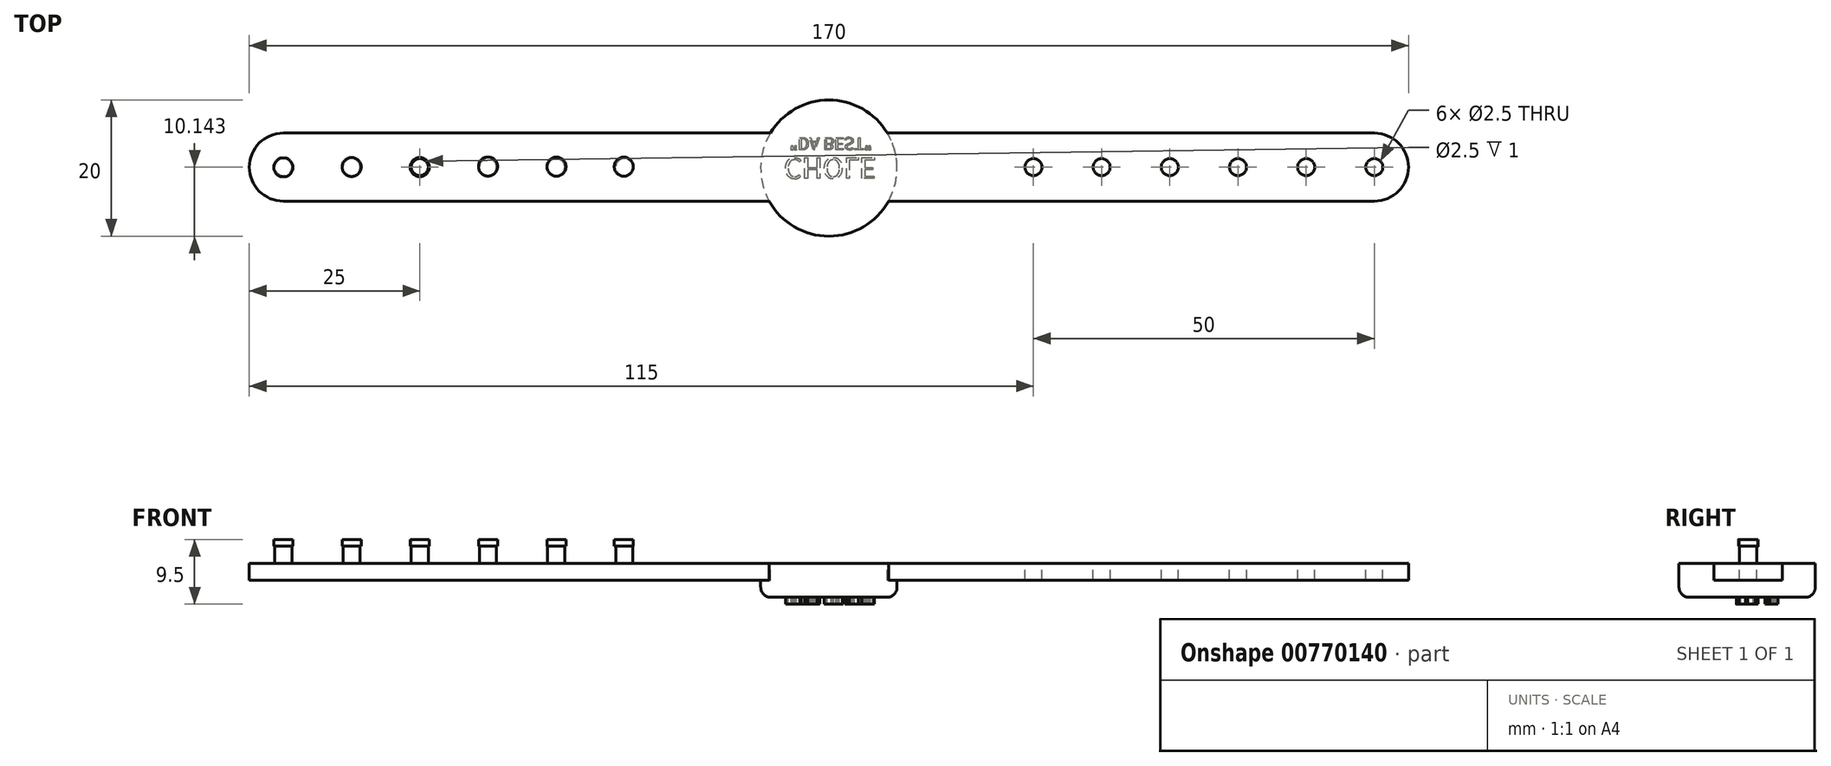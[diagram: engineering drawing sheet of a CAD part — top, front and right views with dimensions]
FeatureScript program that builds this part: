
annotation { "Feature Type Name" : "Feature", "Feature Type Description" : "" }
export const myFeature = defineFeature(function(context is Context, id is Id, definition is map)
    precondition{}
    {
        {
            var Q0;
            Q0=qCreatedBy(makeId("Top.planeOp"),FACE);
            var sketch = newSketch(context, id + "F0", { "sketchPlane" : qUnion([Q0])});
            skLineSegment(sketch, "E0.bottom", {"start": v(-78.4, 24.85) * mm, "end": v(91.6, 24.85) * mm});
            skLineSegment(sketch, "E0.top", {"start": v(-78.4, 14.85) * mm, "end": v(91.6, 14.85) * mm});
            skLineSegment(sketch, "E0.left", {"start": v(-78.4, 24.85) * mm, "end": v(-78.4, 14.85) * mm});
            skLineSegment(sketch, "E0.right", {"start": v(91.6, 24.85) * mm, "end": v(91.6, 14.85) * mm});
            skSolve(sketch);
        }
        {
            var Q0;
            Q0=makeQuery(id+"F0.imprint","IMPRINT",FACE,{"disambiguationData":[TD([[makeQuery(id+"F0.imprint","IMPRINT",EDGE,{"derivedFrom":sQuery(id+"F0.wireOp",EDGE,"E0.bottom")}),-1.0]])]});
            extrude(context, id + "F1", {"entities" : qUnion([Q0]), "depth" : 2.5 * mm, "offsetDistance" : 25 * mm});
        }
        {
            var Q0;
            Q0=makeQuery(id+"F1.opExtrude","SWEPT_EDGE",EDGE,{"disambiguationData":[OSD([sQuery(id+"F0.wireOp",EDGE,"E0.top"),sQuery(id+"F0.wireOp",EDGE,"E0.left")])]});
            var Q1;
            Q1=makeQuery(id+"F1.opExtrude","SWEPT_EDGE",EDGE,{"disambiguationData":[OSD([sQuery(id+"F0.wireOp",EDGE,"E0.bottom"),sQuery(id+"F0.wireOp",EDGE,"E0.left")])]});
            var Q2;
            Q2=makeQuery(id+"F1.opExtrude","SWEPT_EDGE",EDGE,{"disambiguationData":[OSD([sQuery(id+"F0.wireOp",EDGE,"E0.top"),sQuery(id+"F0.wireOp",EDGE,"E0.right")])]});
            var Q3;
            Q3=makeQuery(id+"F1.opExtrude","SWEPT_EDGE",EDGE,{"disambiguationData":[OSD([sQuery(id+"F0.wireOp",EDGE,"E0.bottom"),sQuery(id+"F0.wireOp",EDGE,"E0.right")])]});
            fillet(context, id + "F2", {"entities" : qUnion([Q0, Q1, Q2, Q3]), "radius" : 5 * mm, "tangentPropagation" : true, "allowEdgeOverflow" : false});
        }
        {
            var Q0;
            Q0=makeQuery(id+"F1.opExtrude","CAP_FACE",FACE,{"disambiguationData":[OSD([sQuery(id+"F0.wireOp",EDGE,"E0.bottom"),sQuery(id+"F0.wireOp",EDGE,"E0.top"),sQuery(id+"F0.wireOp",EDGE,"E0.left"),sQuery(id+"F0.wireOp",EDGE,"E0.right")])],"isStart":false});
            var sketch = newSketch(context, id + "F3", { "sketchPlane" : qUnion([Q0])});
            skCircle(sketch, "E1", {"center": v(86.6, 19.85) * mm, "radius": 1.25 * mm});
            skCircle(sketch, "E2", {"center": v(76.6, 19.85) * mm, "radius": 1.25 * mm});
            skCircle(sketch, "E3", {"center": v(66.6, 19.85) * mm, "radius": 1.25 * mm});
            skCircle(sketch, "E4", {"center": v(56.6, 19.85) * mm, "radius": 1.25 * mm});
            skCircle(sketch, "E5", {"center": v(46.6, 19.85) * mm, "radius": 1.25 * mm});
            skCircle(sketch, "E6", {"center": v(36.6, 19.85) * mm, "radius": 1.25 * mm});
            skSolve(sketch);
        }
        {
            var Q0;
            Q0=makeQuery(id+"F3.imprint","IMPRINT",FACE,{"disambiguationData":[TD([[makeQuery(id+"F3.imprint","IMPRINT",EDGE,{"derivedFrom":sQuery(id+"F3.wireOp",EDGE,"E1")}),1.0]])]});
            var Q1;
            Q1=makeQuery(id+"F3.imprint","IMPRINT",FACE,{"disambiguationData":[TD([[makeQuery(id+"F3.imprint","IMPRINT",EDGE,{"derivedFrom":sQuery(id+"F3.wireOp",EDGE,"E2")}),1.0]])]});
            var Q2;
            Q2=makeQuery(id+"F3.imprint","IMPRINT",FACE,{"disambiguationData":[TD([[makeQuery(id+"F3.imprint","IMPRINT",EDGE,{"derivedFrom":sQuery(id+"F3.wireOp",EDGE,"E3")}),1.0]])]});
            var Q3;
            Q3=makeQuery(id+"F3.imprint","IMPRINT",FACE,{"disambiguationData":[TD([[makeQuery(id+"F3.imprint","IMPRINT",EDGE,{"derivedFrom":sQuery(id+"F3.wireOp",EDGE,"E4")}),1.0]])]});
            var Q4;
            Q4=makeQuery(id+"F3.imprint","IMPRINT",FACE,{"disambiguationData":[TD([[makeQuery(id+"F3.imprint","IMPRINT",EDGE,{"derivedFrom":sQuery(id+"F3.wireOp",EDGE,"E5")}),1.0]])]});
            var Q5;
            Q5=makeQuery(id+"F3.imprint","IMPRINT",FACE,{"disambiguationData":[TD([[makeQuery(id+"F3.imprint","IMPRINT",EDGE,{"derivedFrom":sQuery(id+"F3.wireOp",EDGE,"E6")}),1.0]])]});
            extrude(context, id + "F4", {"entities" : qUnion([Q0, Q1, Q2, Q3, Q4, Q5]), "operationType" : NewBodyOperationType.REMOVE, "oppositeDirection" : true, "depth" : 25 * mm, "offsetDistance" : 25 * mm});
        }
        {
            var Q0;
            Q0=makeQuery(id+"F1.opExtrude","CAP_FACE",FACE,{"disambiguationData":[OSD([sQuery(id+"F0.wireOp",EDGE,"E0.bottom"),sQuery(id+"F0.wireOp",EDGE,"E0.top"),sQuery(id+"F0.wireOp",EDGE,"E0.left"),sQuery(id+"F0.wireOp",EDGE,"E0.right")])],"isStart":false});
            var sketch = newSketch(context, id + "F5", { "sketchPlane" : qUnion([Q0])});
            skCircle(sketch, "E7", {"center": v(-73.4, 19.85) * mm, "radius": 1.25 * mm});
            skCircle(sketch, "E8", {"center": v(-63.4, 19.85) * mm, "radius": 1.25 * mm});
            skCircle(sketch, "E9", {"center": v(-53.4, 19.85) * mm, "radius": 1.25 * mm});
            skCircle(sketch, "E10", {"center": v(-43.4, 19.85) * mm, "radius": 1.25 * mm});
            skPoint(sketch, "E11.endSnap0", {"position": v(-48.4, 19.85) * mm});
            skCircle(sketch, "E12", {"center": v(-33.4, 19.85) * mm, "radius": 1.25 * mm});
            skCircle(sketch, "E13", {"center": v(-23.4, 19.85) * mm, "radius": 1.25 * mm});
            skSolve(sketch);
        }
        {
            var Q0;
            Q0=makeQuery(id+"F5.imprint","IMPRINT",FACE,{"disambiguationData":[TD([[makeQuery(id+"F5.imprint","IMPRINT",EDGE,{"derivedFrom":sQuery(id+"F5.wireOp",EDGE,"E13")}),1.0]])]});
            var Q1;
            Q1=makeQuery(id+"F5.imprint","IMPRINT",FACE,{"disambiguationData":[TD([[makeQuery(id+"F5.imprint","IMPRINT",EDGE,{"derivedFrom":sQuery(id+"F5.wireOp",EDGE,"E9")}),1.0]])]});
            var Q2;
            Q2=makeQuery(id+"F5.imprint","IMPRINT",FACE,{"disambiguationData":[TD([[makeQuery(id+"F5.imprint","IMPRINT",EDGE,{"derivedFrom":sQuery(id+"F5.wireOp",EDGE,"E10")}),1.0]])]});
            var Q3;
            Q3=makeQuery(id+"F5.imprint","IMPRINT",FACE,{"disambiguationData":[TD([[makeQuery(id+"F5.imprint","IMPRINT",EDGE,{"derivedFrom":sQuery(id+"F5.wireOp",EDGE,"E12")}),1.0]])]});
            var Q4;
            Q4=makeQuery(id+"F5.imprint","IMPRINT",FACE,{"disambiguationData":[TD([[makeQuery(id+"F5.imprint","IMPRINT",EDGE,{"derivedFrom":sQuery(id+"F5.wireOp",EDGE,"E8")}),1.0]])]});
            var Q5;
            Q5=makeQuery(id+"F5.imprint","IMPRINT",FACE,{"disambiguationData":[TD([[makeQuery(id+"F5.imprint","IMPRINT",EDGE,{"derivedFrom":sQuery(id+"F5.wireOp",EDGE,"E7")}),1.0]])]});
            extrude(context, id + "F6", {"entities" : qUnion([Q0, Q1, Q2, Q3, Q4, Q5]), "operationType" : NewBodyOperationType.ADD, "depth" : 2.5 * mm, "offsetDistance" : 25 * mm});
        }
        {
            var Q0;
            Q0=makeQuery(id+"F6.opExtrude","CAP_FACE",FACE,{"disambiguationData":[OSD([sQuery(id+"F5.wireOp",EDGE,"E9")])],"isStart":false});
            var sketch = newSketch(context, id + "F7", { "sketchPlane" : qUnion([Q0])});
            skCircle(sketch, "E14", {"center": v(-53.4, 19.85) * mm, "radius": 1.4 * mm});
            skCircle(sketch, "E15", {"center": v(-43.4, 19.94) * mm, "radius": 1.4 * mm});
            skCircle(sketch, "E16", {"center": v(-33.34, 19.92) * mm, "radius": 1.4 * mm});
            skCircle(sketch, "E17", {"center": v(-23.48, 19.92) * mm, "radius": 1.4 * mm});
            skCircle(sketch, "E18", {"center": v(-63.4, 19.87) * mm, "radius": 1.4 * mm});
            skCircle(sketch, "E19", {"center": v(-73.4, 19.82) * mm, "radius": 1.4 * mm});
            skSolve(sketch);
        }
        {
            var Q0;
            Q0=makeQuery(id+"F7.imprint","IMPRINT",FACE,{"disambiguationData":[TD([[makeQuery(id+"F7.imprint","IMPRINT",EDGE,{"derivedFrom":sQuery(id+"F7.wireOp",EDGE,"E19")}),1.0]])]});
            var Q1;
            Q1=makeQuery(id+"F7.imprint","IMPRINT",FACE,{"disambiguationData":[TD([[makeQuery(id+"F7.imprint","IMPRINT",EDGE,{"derivedFrom":sQuery(id+"F7.wireOp",EDGE,"E18")}),1.0]])]});
            var Q2;
            Q2=makeQuery(id+"F7.imprint","IMPRINT",FACE,{"disambiguationData":[TD([[makeQuery(id+"F7.imprint","IMPRINT",EDGE,{"derivedFrom":sQuery(id+"F7.wireOp",EDGE,"E14")}),1.0]])]});
            var Q3;
            Q3=makeQuery(id+"F7.imprint","IMPRINT",FACE,{"disambiguationData":[TD([[makeQuery(id+"F7.imprint","IMPRINT",EDGE,{"derivedFrom":sQuery(id+"F7.wireOp",EDGE,"E15")}),1.0]])]});
            var Q4;
            Q4=makeQuery(id+"F7.imprint","IMPRINT",FACE,{"disambiguationData":[TD([[makeQuery(id+"F7.imprint","IMPRINT",EDGE,{"derivedFrom":sQuery(id+"F7.wireOp",EDGE,"E16")}),1.0]])]});
            var Q5;
            Q5=makeQuery(id+"F7.imprint","IMPRINT",FACE,{"disambiguationData":[TD([[makeQuery(id+"F7.imprint","IMPRINT",EDGE,{"derivedFrom":sQuery(id+"F7.wireOp",EDGE,"E17")}),1.0]])]});
            extrude(context, id + "F8", {"entities" : qUnion([Q0, Q1, Q2, Q3, Q4, Q5]), "operationType" : NewBodyOperationType.ADD, "depth" : 1 * mm, "offsetDistance" : 25 * mm});
        }
        {
            var Q0;
            Q0=makeQuery(id+"F6.opExtrude","CAP_FACE",FACE,{"disambiguationData":[OSD([sQuery(id+"F5.wireOp",EDGE,"E9")])],"isStart":false});
            extrude(context, id + "F9", {"entities" : qUnion([Q0]), "depth" : 1 * mm, "offsetDistance" : 25 * mm});
        }
        {
            var Q0;
            Q0=makeQuery(id+"F1.opExtrude","CAP_FACE",FACE,{"disambiguationData":[OSD([sQuery(id+"F0.wireOp",EDGE,"E0.bottom"),sQuery(id+"F0.wireOp",EDGE,"E0.top"),sQuery(id+"F0.wireOp",EDGE,"E0.left"),sQuery(id+"F0.wireOp",EDGE,"E0.right")])],"isStart":false});
            var sketch = newSketch(context, id + "F10", { "sketchPlane" : qUnion([Q0])});
            skCircle(sketch, "E20", {"center": v(6.6, 19.7) * mm, "radius": 10 * mm});
            skPoint(sketch, "E20.centerSnap0", {"position": v(6.6, 24.85) * mm});
            skSolve(sketch);
        }
        {
            var Q0;
            {var subQ0=sQuery(id+"F10.wireOp",EDGE,"E20");var subQ1=makeQuery(id+"F1.opExtrude","CAP_EDGE",EDGE,{"disambiguationData":[OSD([sQuery(id+"F0.wireOp",EDGE,"E0.bottom")])],"isStart":false});var subQ2=makeQuery(id+"F10.imprint","INTERSECT",VERTEX,{"disambiguationData":[OD(0.0)],"derivedFrom":[subQ1,subQ0]});Q0=makeQuery(id+"F10.imprint","IMPRINT",FACE,{"disambiguationData":[TD([[makeQuery(id+"F10.imprint","IMPRINT",EDGE,{"disambiguationData":[TD([[subQ2,-1.0]])],"derivedFrom":subQ0}),1.0]])]});}
            var Q1;
            {var subQ0=sQuery(id+"F10.wireOp",EDGE,"E20");var subQ1=makeQuery(id+"F1.opExtrude","CAP_EDGE",EDGE,{"disambiguationData":[OSD([sQuery(id+"F0.wireOp",EDGE,"E0.top")])],"isStart":false});var subQ2=makeQuery(id+"F10.imprint","INTERSECT",VERTEX,{"disambiguationData":[OD(0.0)],"derivedFrom":[subQ1,subQ0]});Q1=makeQuery(id+"F10.imprint","IMPRINT",FACE,{"disambiguationData":[TD([[makeQuery(id+"F10.imprint","IMPRINT",EDGE,{"disambiguationData":[TD([[subQ2,-1.0]])],"derivedFrom":subQ0}),1.0]])]});}
            var Q2;
            {var subQ0=sQuery(id+"F10.wireOp",EDGE,"E20");var subQ1=makeQuery(id+"F1.opExtrude","CAP_EDGE",EDGE,{"disambiguationData":[OSD([sQuery(id+"F0.wireOp",EDGE,"E0.bottom")])],"isStart":false});var subQ2=makeQuery(id+"F10.imprint","INTERSECT",VERTEX,{"disambiguationData":[OD(0.0)],"derivedFrom":[subQ1,subQ0]});Q2=makeQuery(id+"F10.imprint","IMPRINT",FACE,{"disambiguationData":[TD([[makeQuery(id+"F10.imprint","IMPRINT",EDGE,{"disambiguationData":[TD([[subQ2,1.0]])],"derivedFrom":subQ0}),1.0]])]});}
            extrude(context, id + "F11", {"entities" : qUnion([Q0, Q1, Q2]), "operationType" : NewBodyOperationType.ADD, "depth" : 2.5 * mm, "offsetDistance" : 25 * mm});
        }
        {
            var Q0;
            {var subQ0=sQuery(id+"F0.wireOp",EDGE,"E0.top");var subQ1=sQuery(id+"F10.wireOp",EDGE,"E20");Q0=makeQuery(id+"F11.boolean.opBoolean","SPLIT",FACE,{"disambiguationData":[TD([makeQuery(id+"F1.opExtrude","SWEPT_FACE",FACE,{"disambiguationData":[OSD([subQ0])]})])],"derivedFrom":makeQuery(id+"F11.opExtrude","CAP_FACE",FACE,{"disambiguationData":[OSD([subQ1])],"isStart":true})});}
            var Q1;
            {var subQ0=sQuery(id+"F0.wireOp",EDGE,"E0.bottom");var subQ1=sQuery(id+"F10.wireOp",EDGE,"E20");Q1=makeQuery(id+"F11.boolean.opBoolean","SPLIT",FACE,{"disambiguationData":[TD([makeQuery(id+"F1.opExtrude","SWEPT_FACE",FACE,{"disambiguationData":[OSD([subQ0])]})])],"derivedFrom":makeQuery(id+"F11.opExtrude","CAP_FACE",FACE,{"disambiguationData":[OSD([subQ1])],"isStart":true})});}
            extrude(context, id + "F12", {"entities" : qUnion([Q0, Q1]), "operationType" : NewBodyOperationType.ADD, "depth" : 2.5 * mm, "offsetDistance" : 25 * mm});
        }
        {
            var Q0;
            Q0=makeQuery(id+"F11.opExtrude","CAP_FACE",FACE,{"disambiguationData":[OSD([sQuery(id+"F10.wireOp",EDGE,"E20")])],"isStart":false});
            extrude(context, id + "F13", {"entities" : qUnion([Q0]), "operationType" : NewBodyOperationType.ADD, "oppositeDirection" : true, "depth" : 7.5 * mm, "offsetDistance" : 25 * mm});
        }
        {
            var Q0;
            Q0=makeQuery(id+"F11.opExtrude","CAP_FACE",FACE,{"disambiguationData":[OSD([sQuery(id+"F10.wireOp",EDGE,"E20")])],"isStart":false});
            extrude(context, id + "F14", {"entities" : qUnion([Q0]), "operationType" : NewBodyOperationType.REMOVE, "oppositeDirection" : true, "depth" : 2.5 * mm, "offsetDistance" : 25 * mm});
        }
        {
            var Q0;
            Q0=makeQuery(id+"F13.opExtrude","CAP_EDGE",EDGE,{"disambiguationData":[OSD([sQuery(id+"F10.wireOp",EDGE,"E20")])],"isStart":false});
            fillet(context, id + "F15", {"entities" : qUnion([Q0]), "radius" : 1.5 * mm, "tangentPropagation" : true, "allowEdgeOverflow" : false});
        }
        {
            var Q0;
            Q0=makeQuery(id+"F13.opExtrude","CAP_FACE",FACE,{"disambiguationData":[OSD([sQuery(id+"F10.wireOp",EDGE,"E20")])],"isStart":false});
            var sketch = newSketch(context, id + "F16", { "sketchPlane" : qUnion([Q0])});
            skText(sketch, "E21", { "text": "CHOLE", "fontName": "NotoSansCJKkr-Regular.otf"});
            const initialGuessF16  = {"E21": [0, -0.02123, 1, 0, 0.003]};
            skSetInitialGuess(sketch, initialGuessF16);
            skSolve(sketch);
        }
        {
            var Q0;
            Q0 = qSketchRegion(id + "F16", true);
            extrude(context, id + "F17", {"entities" : qUnion([Q0]), "operationType" : NewBodyOperationType.ADD, "depth" : 1 * mm, "offsetDistance" : 25 * mm});
        }
        {
            var Q0;
            {var subQ0=sQuery(id+"F10.wireOp",EDGE,"E20");Q0=makeQuery(id+"F17.boolean.opBoolean","SPLIT",FACE,{"disambiguationData":[TD([makeQuery(id+"F15.opFillet","BLEND_FACE",FACE,{"disambiguationData":[OSD([subQ0])]})])],"derivedFrom":makeQuery(id+"F13.opExtrude","CAP_FACE",FACE,{"disambiguationData":[OSD([subQ0])],"isStart":false})});}
            var sketch = newSketch(context, id + "F18", { "sketchPlane" : qUnion([Q0])});
            skText(sketch, "E22", { "text": "\"DA BEST\"", "fontName": "NotoSansCJKkr-Regular.otf"});
            const initialGuessF18  = {"E22": [0.00087, -0.0242, 1, 0, 0.00177]};
            skSetInitialGuess(sketch, initialGuessF18);
            skSolve(sketch);
        }
        {
            var Q0;
            Q0 = qSketchRegion(id + "F18", true);
            extrude(context, id + "F19", {"entities" : qUnion([Q0]), "operationType" : NewBodyOperationType.ADD, "depth" : 1 * mm, "offsetDistance" : 25 * mm});
        }
    });
